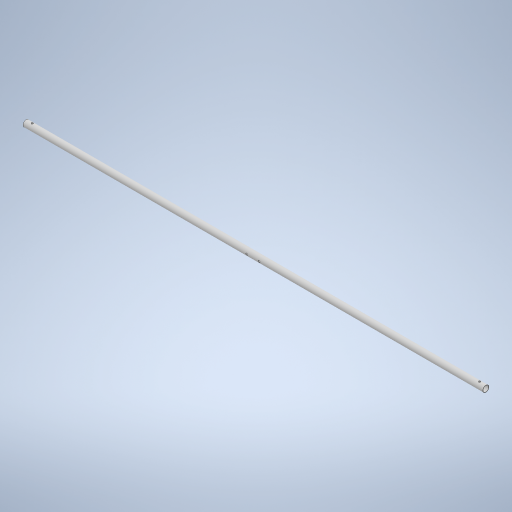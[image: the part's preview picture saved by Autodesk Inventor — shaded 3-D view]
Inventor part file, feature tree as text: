
AUTODESK INVENTOR PART (.ipt)
format: ipt  version: 2024 (Build 280153000, 153)  size: 274,944 bytes
history: native  units: mm
features: extrude x3, sketch x3, other x1
ambient origin geometry x8: Origin, YZ Plane, XZ Plane, XY Plane, X Axis, Y Axis, Z Axis, Center Point
bodies: Body1 (feature_tree)
feature tree (7):
  other  "솔리드1"
  extrude  "돌출1"  Depth=10.0mm
  extrude  "돌출2"  Depth=9.0mm
  extrude  "돌출3"  Depth=740.0mm TaperAngle=0.0deg
  sketch  "스케치1"
  sketch  "스케치2"
  sketch  "스케치3"
